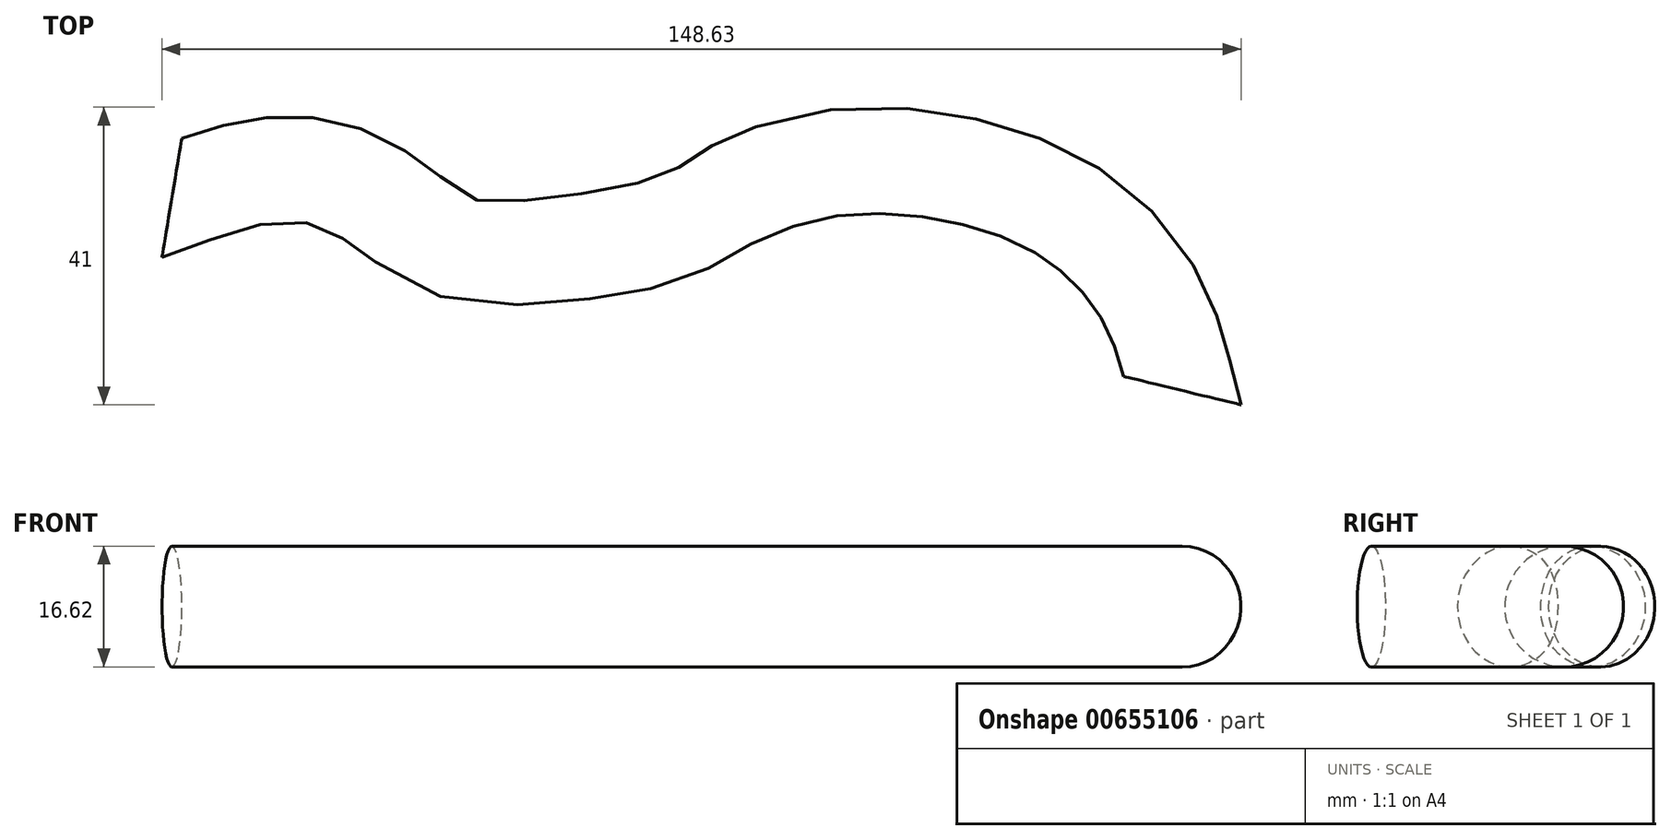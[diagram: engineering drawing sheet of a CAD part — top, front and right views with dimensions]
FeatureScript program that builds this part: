
annotation { "Feature Type Name" : "Feature", "Feature Type Description" : "" }
export const myFeature = defineFeature(function(context is Context, id is Id, definition is map)
    precondition{}
    {
        {
            var Q0;
            Q0=qCreatedBy(makeId("Top.planeOp"),FACE);
            var sketch = newSketch(context, id + "F0", { "sketchPlane" : qUnion([Q0])});
            skFitSpline(sketch, "E0", {"points": [v(-74.58, 0) * mm, v(-61.08, 3.65) * mm, v(-49.47, 1.78) * mm, v(-38.6, -4.97) * mm, v(-26.8, -7.21) * mm, v(-6.75, -4.22) * mm, v(2.06, 0) * mm, v(18.55, 4.97) * mm, v(45.35, 0) * mm, v(59.02, -12.65) * mm, v(63.7, -25.2) * mm], "startDerivative": vector(142.84, 50.32) * mm, "endDerivative": vector(37.1, -135.97) * mm});
            skSolve(sketch);
        }
        {
            var Q0;
            Q0=qCreatedBy(makeId("Right.planeOp"),FACE);
            var sketch = newSketch(context, id + "F1", { "sketchPlane" : qUnion([Q0])});
            skCircle(sketch, "E1", {"center": v(0, 0) * mm, "radius": 8.31 * mm});
            skSolve(sketch);
        }
        {
            var Q0;
            Q0=makeQuery(id+"F1.imprint","IMPRINT",FACE,{"disambiguationData":[TD([[makeQuery(id+"F1.imprint","IMPRINT",EDGE,{"derivedFrom":sQuery(id+"F1.wireOp",EDGE,"E1")}),1.0]])]});
            var Q1;
            Q1=sQuery(id+"F0.wireOp",EDGE,"E0");
            sweep(context, id + "F2", {"profiles" : qUnion([Q0]), "path" : qUnion([Q1])});
        }
    });
